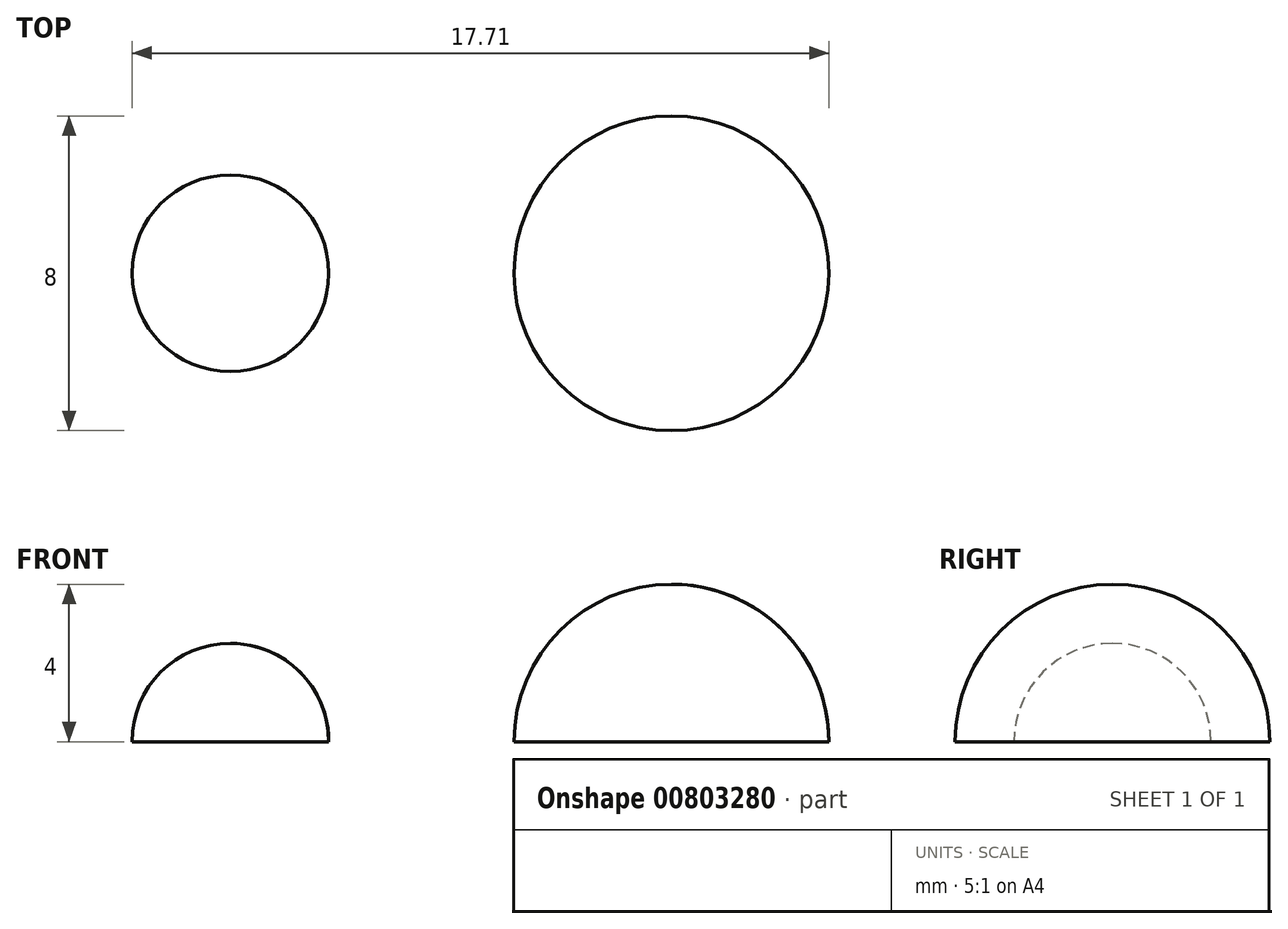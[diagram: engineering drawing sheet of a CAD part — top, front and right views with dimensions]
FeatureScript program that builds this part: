
annotation { "Feature Type Name" : "Feature", "Feature Type Description" : "" }
export const myFeature = defineFeature(function(context is Context, id is Id, definition is map)
    precondition{}
    {
        {
            var Q0;
            Q0=qCreatedBy(makeId("Top.planeOp"),FACE);
            var sketch = newSketch(context, id + "F0", { "sketchPlane" : qUnion([Q0])});
            skCircle(sketch, "E0", {"center": v(0, 0) * mm, "radius": 2.5 * mm});
            skCircle(sketch, "E1", {"center": v(11.2, 0) * mm, "radius": 4 * mm});
            skSolve(sketch);
        }
        {
            var Q0;
            Q0=makeQuery(id+"F0.imprint","IMPRINT",FACE,{"disambiguationData":[TD([[makeQuery(id+"F0.imprint","IMPRINT",EDGE,{"derivedFrom":sQuery(id+"F0.wireOp",EDGE,"E0")}),1.0]])]});
            extrude(context, id + "F1", {"entities" : qUnion([Q0]), "depth" : 2.5 * mm, "offsetDistance" : 25 * mm});
        }
        {
            var Q0;
            Q0=makeQuery(id+"F0.imprint","IMPRINT",FACE,{"disambiguationData":[TD([[makeQuery(id+"F0.imprint","IMPRINT",EDGE,{"derivedFrom":sQuery(id+"F0.wireOp",EDGE,"E1")}),1.0]])]});
            extrude(context, id + "F2", {"entities" : qUnion([Q0]), "depth" : 4 * mm, "offsetDistance" : 25 * mm});
        }
        {
            var Q0;
            Q0=makeQuery(id+"F1.opExtrude","CAP_FACE",FACE,{"disambiguationData":[OSD([sQuery(id+"F0.wireOp",EDGE,"E0")])],"isStart":false});
            fillet(context, id + "F3", {"entities" : qUnion([Q0]), "radius" : 2.5 * mm, "tangentPropagation" : true, "allowEdgeOverflow" : false});
        }
        {
            var Q0;
            Q0=makeQuery(id+"F2.opExtrude","CAP_FACE",FACE,{"disambiguationData":[OSD([sQuery(id+"F0.wireOp",EDGE,"E1")])],"isStart":false});
            fillet(context, id + "F4", {"entities" : qUnion([Q0]), "radius" : 4 * mm, "tangentPropagation" : true, "allowEdgeOverflow" : false});
        }
    });
